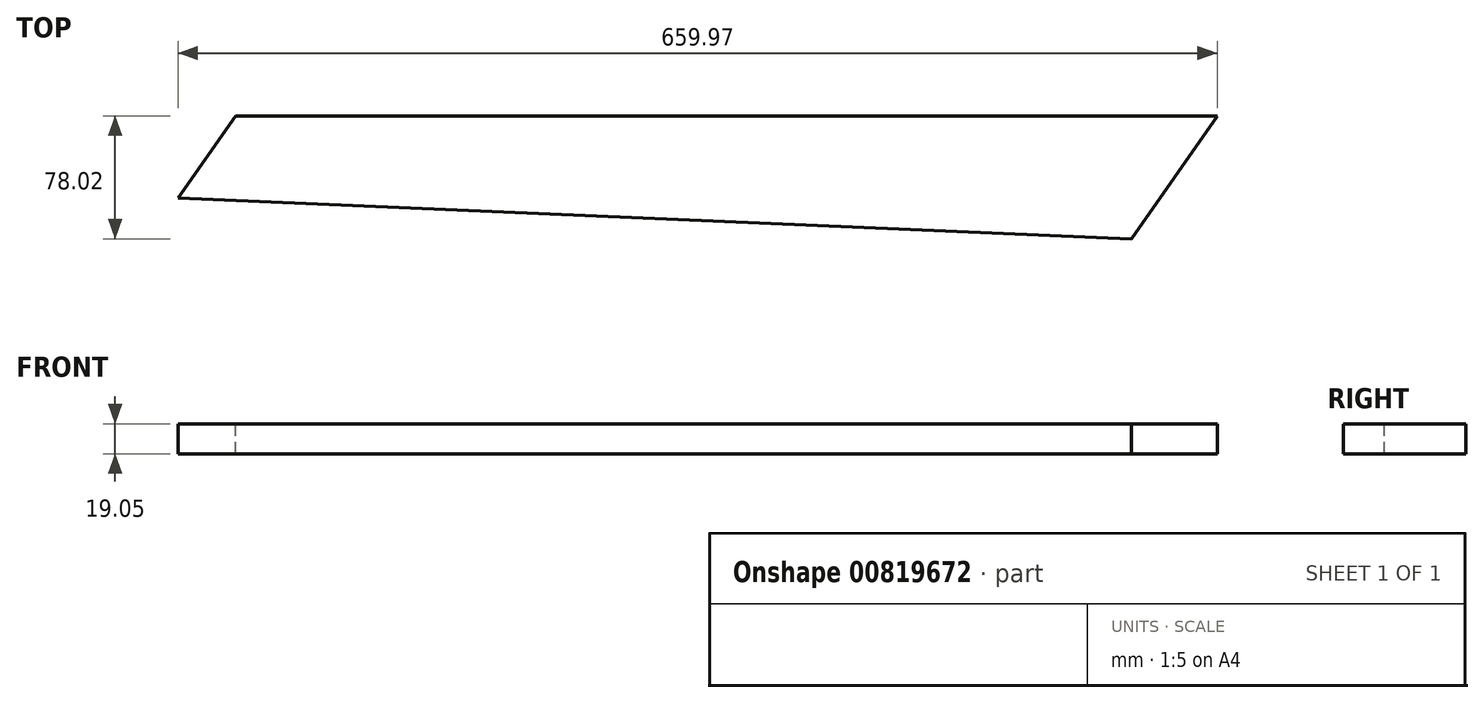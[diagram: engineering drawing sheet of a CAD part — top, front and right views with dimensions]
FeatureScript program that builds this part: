
annotation { "Feature Type Name" : "Feature", "Feature Type Description" : "" }
export const myFeature = defineFeature(function(context is Context, id is Id, definition is map)
    precondition{}
    {
        {
            var Q0;
            Q0=qCreatedBy(makeId("Front.planeOp"),FACE);
            var sketch = newSketch(context, id + "F0", { "sketchPlane" : qUnion([Q0])});
            skLineSegment(sketch, "E0.bottom", {"start": v(0, 0) * mm, "end": v(-685.8, 0) * mm});
            skLineSegment(sketch, "E0.top", {"start": v(0, 19.05) * mm, "end": v(-685.8, 19.05) * mm});
            skLineSegment(sketch, "E0.left", {"start": v(0, 0) * mm, "end": v(0, 19.05) * mm});
            skLineSegment(sketch, "E0.right", {"start": v(-685.8, 0) * mm, "end": v(-685.8, 19.05) * mm});
            skSolve(sketch);
        }
        {
            var Q0;
            Q0=makeQuery(id+"F0.imprint","IMPRINT",FACE,{"disambiguationData":[TD([[makeQuery(id+"F0.imprint","IMPRINT",EDGE,{"derivedFrom":sQuery(id+"F0.wireOp",EDGE,"E0.bottom")}),-1.0]])]});
            extrude(context, id + "F1", {"entities" : qUnion([Q0]), "depth" : 88.9 * mm, "offsetDistance" : 25.4 * mm});
        }
        {
            var Q0;
            Q0=makeQuery(id+"F1.opExtrude","SWEPT_FACE",FACE,{"disambiguationData":[OSD([sQuery(id+"F0.wireOp",EDGE,"E0.top")])]});
            var sketch = newSketch(context, id + "F2", { "sketchPlane" : qUnion([Q0])});
            skLineSegment(sketch, "E1", {"start": v(0, 0) * mm, "end": v(-62.25, -88.9) * mm});
            skLineSegment(sketch, "E2", {"start": v(-62.25, -88.9) * mm, "end": v(0, -88.9) * mm});
            skLineSegment(sketch, "E3", {"start": v(0, -88.9) * mm, "end": v(0, 0) * mm});
            skSolve(sketch);
        }
        {
            var Q0;
            Q0 = qSketchRegion(id + "F2", true);
            extrude(context, id + "F3", {"entities" : qUnion([Q0]), "operationType" : NewBodyOperationType.REMOVE, "oppositeDirection" : true, "depth" : 127 * mm, "offsetDistance" : 25.4 * mm});
        }
        {
            var Q0;
            Q0=makeQuery(id+"F1.opExtrude","SWEPT_FACE",FACE,{"disambiguationData":[OSD([sQuery(id+"F0.wireOp",EDGE,"E0.top")])]});
            var sketch = newSketch(context, id + "F4", { "sketchPlane" : qUnion([Q0])});
            skLineSegment(sketch, "E4", {"start": v(-685.8, -88.9) * mm, "end": v(-623.55, 0) * mm});
            skLineSegment(sketch, "E5", {"start": v(-623.55, 0) * mm, "end": v(-685.8, 0) * mm});
            skLineSegment(sketch, "E6", {"start": v(-685.8, 0) * mm, "end": v(-685.8, -88.9) * mm});
            skSolve(sketch);
        }
        {
            var Q0;
            Q0=makeQuery(id+"F4.imprint","IMPRINT",FACE,{"disambiguationData":[TD([[makeQuery(id+"F4.imprint","IMPRINT",EDGE,{"derivedFrom":sQuery(id+"F4.wireOp",EDGE,"E4")}),1.0]])]});
            extrude(context, id + "F5", {"entities" : qUnion([Q0]), "operationType" : NewBodyOperationType.REMOVE, "oppositeDirection" : true, "depth" : 127 * mm, "offsetDistance" : 25.4 * mm});
        }
        {
            var Q0;
            Q0=makeQuery(id+"F1.opExtrude","SWEPT_FACE",FACE,{"disambiguationData":[OSD([sQuery(id+"F0.wireOp",EDGE,"E0.top")])]});
            var sketch = newSketch(context, id + "F6", { "sketchPlane" : qUnion([Q0])});
            skLineSegment(sketch, "E7", {"start": v(-623.55, 0) * mm, "end": v(-659.97, -52.02) * mm, "construction": true});
            skLineSegment(sketch, "E8", {"start": v(-62.25, -88.9) * mm, "end": v(-685.8, -88.9) * mm});
            skLineSegment(sketch, "E9", {"start": v(-685.8, -88.9) * mm, "end": v(-659.97, -52.02) * mm});
            skLineSegment(sketch, "E10", {"start": v(0, 0) * mm, "end": v(-54.63, -78.02) * mm, "construction": true});
            skLineSegment(sketch, "E11", {"start": v(-659.97, -52.02) * mm, "end": v(-54.63, -78.02) * mm});
            skLineSegment(sketch, "E12", {"start": v(-54.63, -78.02) * mm, "end": v(-62.25, -88.9) * mm});
            skSolve(sketch);
        }
        {
            var Q0;
            Q0 = qSketchRegion(id + "F6", true);
            extrude(context, id + "F7", {"entities" : qUnion([Q0]), "operationType" : NewBodyOperationType.REMOVE, "oppositeDirection" : true, "depth" : 25.4 * mm, "offsetDistance" : 25.4 * mm});
        }
    });
